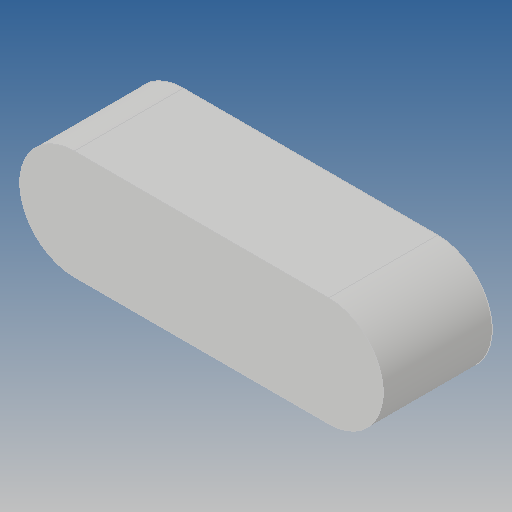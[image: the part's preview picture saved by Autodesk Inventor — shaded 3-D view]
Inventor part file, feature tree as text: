
AUTODESK INVENTOR PART (.ipt)
format: ipt  version: 2018 (Build 220112000, 112)  size: 90,624 bytes
history: native  units: mm
features: extrude x1
ambient origin geometry x8: Origin, YZ Plane, XZ Plane, XY Plane, X Axis, Y Axis, Z Axis, Center Point
bodies: Solid1 (feature_tree)
feature tree (1):
  extrude  "Extrude2"  [1 undecoded]
note: 1 required parameter value undecoded (feature->parameter linkage not recoverable at this tier; creation-order binding heuristic only, values carry confidence <= 0.55)
